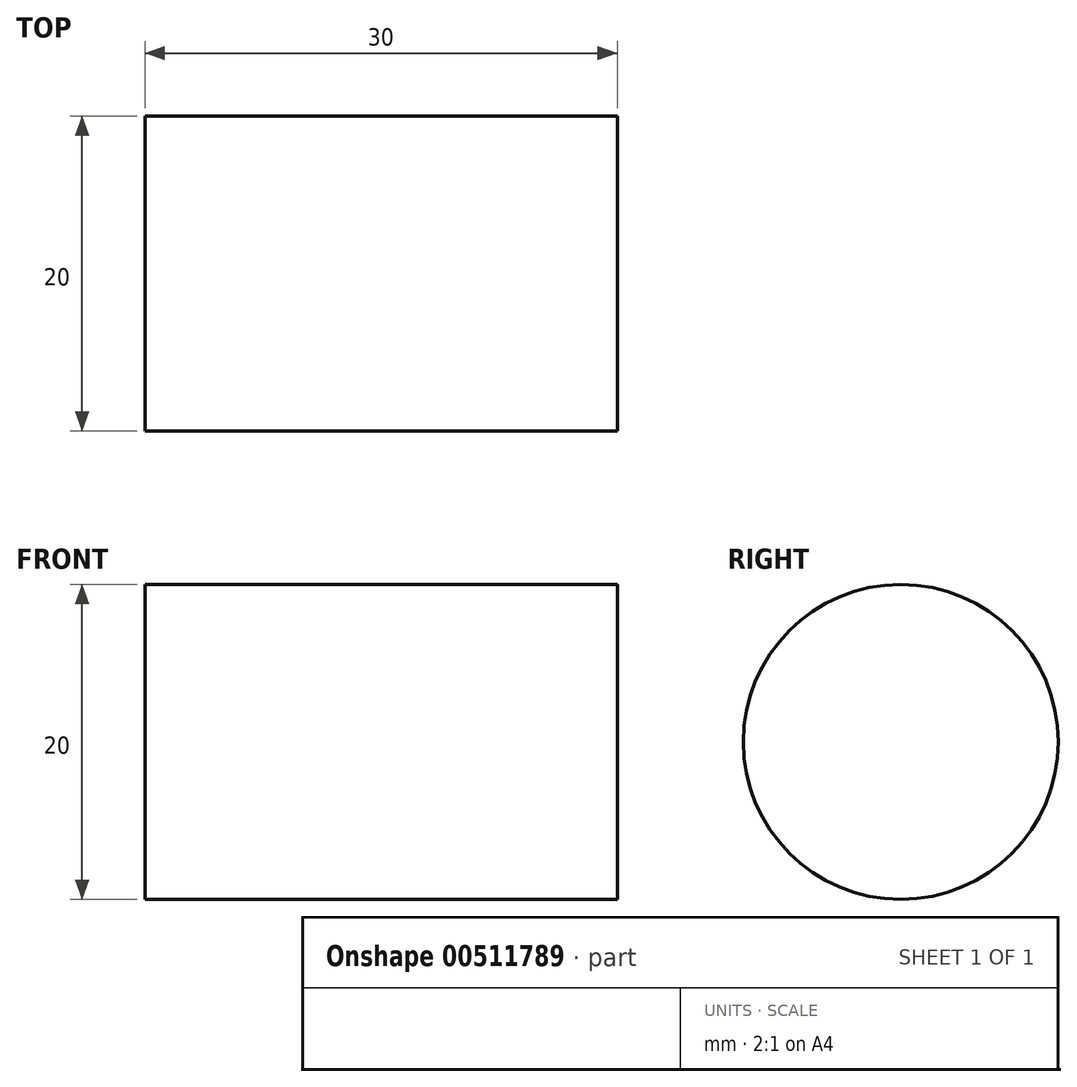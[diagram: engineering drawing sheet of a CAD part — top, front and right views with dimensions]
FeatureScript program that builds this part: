
annotation { "Feature Type Name" : "Feature", "Feature Type Description" : "" }
export const myFeature = defineFeature(function(context is Context, id is Id, definition is map)
    precondition{}
    {
        {
            var Q0;
            Q0=qCreatedBy(makeId("Right.planeOp"),FACE);
            var sketch = newSketch(context, id + "F0", { "sketchPlane" : qUnion([Q0])});
            skCircle(sketch, "E0", {"center": v(0, 0) * mm, "radius": 10 * mm});
            skSolve(sketch);
        }
        {
            var Q0;
            Q0 = qSketchRegion(id + "F0", true);
            extrude(context, id + "F1", {"entities" : qUnion([Q0]), "depth" : 30 * mm});
        }
    });
